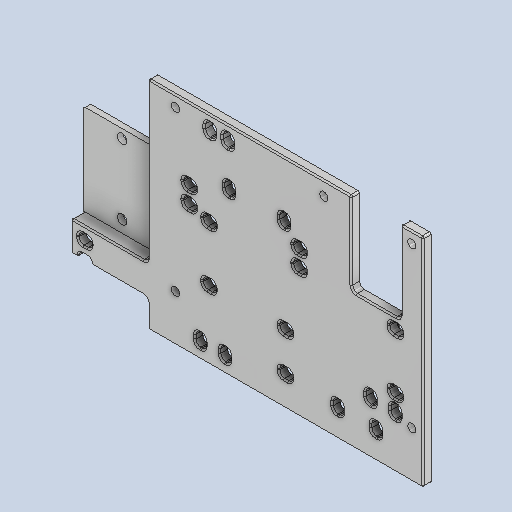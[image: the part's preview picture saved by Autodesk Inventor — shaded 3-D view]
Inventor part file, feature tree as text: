
AUTODESK INVENTOR PART (.ipt)
format: ipt  version: 2024.2 (Build 282272000, 272)  size: 1,372,160 bytes
history: native  units: mm
features: extrude x16, fillet x11, sketch x10, projected_geometry x5, chamfer x1
ambient origin geometry x8: Origin, YZ Plane, XZ Plane, XY Plane, X Axis, Y Axis, Z Axis, Center Point
bodies: Solid1 (feature_tree)
feature tree (43):
  extrude  "Extrusion1"  Depth=79.0mm
  extrude  "Extrusion2"  Depth=3.0mm
  fillet  "Fillet1"  Radius=3.0mm
  extrude  "Extrusion3"  Depth=4.0mm
  extrude  "Extrusion4"  Depth=4.0mm
  extrude  "Extrusion5"  Depth=2.0mm TaperAngle=0.0deg
  extrude  "Extrusion6"  Depth=4.0mm
  fillet  "Fillet2"  Radius=4.0mm
  fillet  "Fillet3"  Radius=4.0mm
  fillet  "Fillet4"  Radius=4.0mm
  extrude  "Extrusion7"  Depth=4.0mm
  extrude  "Extrusion8"  Depth=4.0mm
  fillet  "Fillet5"  Radius=4.0mm
  extrude  "Extrusion9"  Depth=5.0mm
  fillet  "Fillet6"  Radius=5.0mm
  sketch  "Sketch11"  dims[d10=33.0mm d11=2.0mm d12=0.0mm]
  extrude  "Extrusion10"  Depth=5.0mm
  extrude  "Extrusion11"  Depth=5.0mm
  extrude  "Extrusion12"  Depth=5.0mm
  fillet  "Fillet7"  Radius=5.0mm
  extrude  "Extrusion13"  Depth=5.0mm
  extrude  "Extrusion14"  TaperAngle=0.0deg  [1 undecoded]
  fillet  "Fillet8"  Radius=20.0mm
  fillet  "Fillet9"  Radius=20.0mm
  extrude  "Extrusion15"  Depth=14.0mm
  fillet  "Fillet10"  Radius=14.0mm
  extrude  "Extrusion16"  Depth=17.0mm
  fillet  "Fillet11"  Radius=10.0mm
  chamfer  "Chamfer1"  Distance=25.0mm
  sketch  "Sketch2"  dims[d0=100.0mm d1=79.0mm]
  sketch  "Sketch3"  dims[d2=3.0mm d3=0.0mm d4=3.0mm d5=3.0mm]
  projected_geometry  "Projected Loop1"
  sketch  "Sketch9"  dims[d6=86.0mm d7=4.0mm]
  projected_geometry  "Projected Loop2"
  sketch  "Sketch10"  dims[d8=4.0mm d9=4.0mm]
  projected_geometry  "Projected Loop3"
  sketch  "Sketch12"  dims[d13=0.6mm d14=4.0mm d15=4.0mm d16=4.0mm d17=4.0mm]
  projected_geometry  "Projected Loop4"
  sketch  "Sketch13"  dims[d18=4.0mm d19=4.0mm]
  projected_geometry  "Projected Loop5"
  sketch  "Sketch14"  dims[d20=4.0mm d21=4.0mm d23=4.0mm]
  sketch  "Sketch15"  dims[d24=5.0mm d25=5.0mm d26=5.0mm]
  sketch  "Sketch16"  dims[d27=5.0mm d29=5.0mm d30=5.0mm d31=5.0mm d32=5.0mm d33=5.0mm d34=0.0mm d35=20.0mm d36=20.0mm d37=14.0mm d38=14.0mm d40=17.0mm d41=10.0mm d42=25.0mm d43=50.0mm d44=34.0mm d45=4.0mm d46=5.0mm d47=20.0mm d48=0.0mm d49=0.0mm d50=10.0mm d51=0.0mm d52=0.0mm d54=4.0mm d55=5.0mm d56=4.0mm d57=5.0mm d60=4.0mm d61=5.0mm d62=2.0mm d63=5.0mm d64=0.0mm d65=5.0mm d66=19.0mm d67=6.0mm d72=4.0mm d73=5.0mm d74=4.0mm d75=5.0mm d76=0.0mm d77=5.0mm d78=2.0mm d79=5.0mm d80=2.0mm d81=5.0mm d82=10.022273mm d83=2.022273mm d84=4.0mm d85=0.0mm d86=0.0mm d87=5.0mm d88=4.0mm d89=4.0mm d90=4.0mm d91=5.0mm d92=5.0mm d93=6.0mm d98=3.5mm d102=26.0mm d103=15.0mm d105=4.0mm d106=4.0mm d107=5.0mm d108=5.0mm d109=6.0mm d116=2.0mm d117=5.0mm d121=0.0mm d122=45.0mm d123=0.0mm d124=0.0mm d125=20.0mm d126=29.5mm d127=30.0mm d128=8.0mm d129=18.0mm d130=0.0mm d131=0.0mm d132=0.6mm d133=1.75mm d134=1.75mm d135=1.75mm d136=3.0mm d137=5.0mm d138=10.0mm d139=10.0mm d140=0.0mm d141=0.5mm d142=2.0mm d143=45.0deg d145=8.0mm d146=12.2mm d147=41.0mm d148=1.5mm d149=0.0mm d151=28.5mm d152=1.75mm d153=21.0mm d154=33.0mm d155=2.25mm d156=0.0mm d157=1.75mm d158=54.0mm d159=3.0mm d160=28.0mm d161=2.25mm d162=0.0mm d163=33.0mm d164=3.6mm d165=0.0mm d166=4.6mm d167=0.0mm d168=1.75mm d169=3.5mm d170=3.5mm d171=25.4mm d172=3.175mm d173=0.0mm d174=0.0mm d175=10.0mm d176=0.0mm d177=0.0mm d178=1.75mm d179=0.6mm d180=2.0mm d181=10.0mm d182=0.0mm d183=0.6mm d187=1.75mm d188=1.5mm d189=0.5mm d190=5.0mm d193=10.0mm d194=0.0mm d195=0.6mm d196=2.5mm d197=2.5mm d198=1.75mm d199=0.5mm d200=0.5mm d201=1.5mm d202=1.5mm d203=22.5mm d204=5.0mm]
note: 1 required parameter value undecoded (feature->parameter linkage not recoverable at this tier; creation-order binding heuristic only, values carry confidence <= 0.55)
